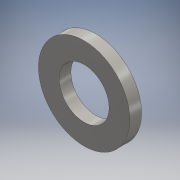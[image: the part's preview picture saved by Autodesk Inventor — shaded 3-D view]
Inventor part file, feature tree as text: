
AUTODESK INVENTOR PART (.ipt)
format: ipt  version: 2016 (Build 200138000, 138)  size: 111,104 bytes
history: native  units: mm
features: extrude x1, sketch x1
ambient origin geometry x8: Origin, YZ Plane, XZ Plane, XY Plane, X Axis, Y Axis, Z Axis, Center Point
bodies: Solid1 (feature_tree)
feature tree (2):
  extrude  "Extrusion1"  Depth=1.5mm
  sketch  "Sketch1"  dims[d0=6.4mm d1=11.7mm d2=1.5mm d3=0.0mm]
